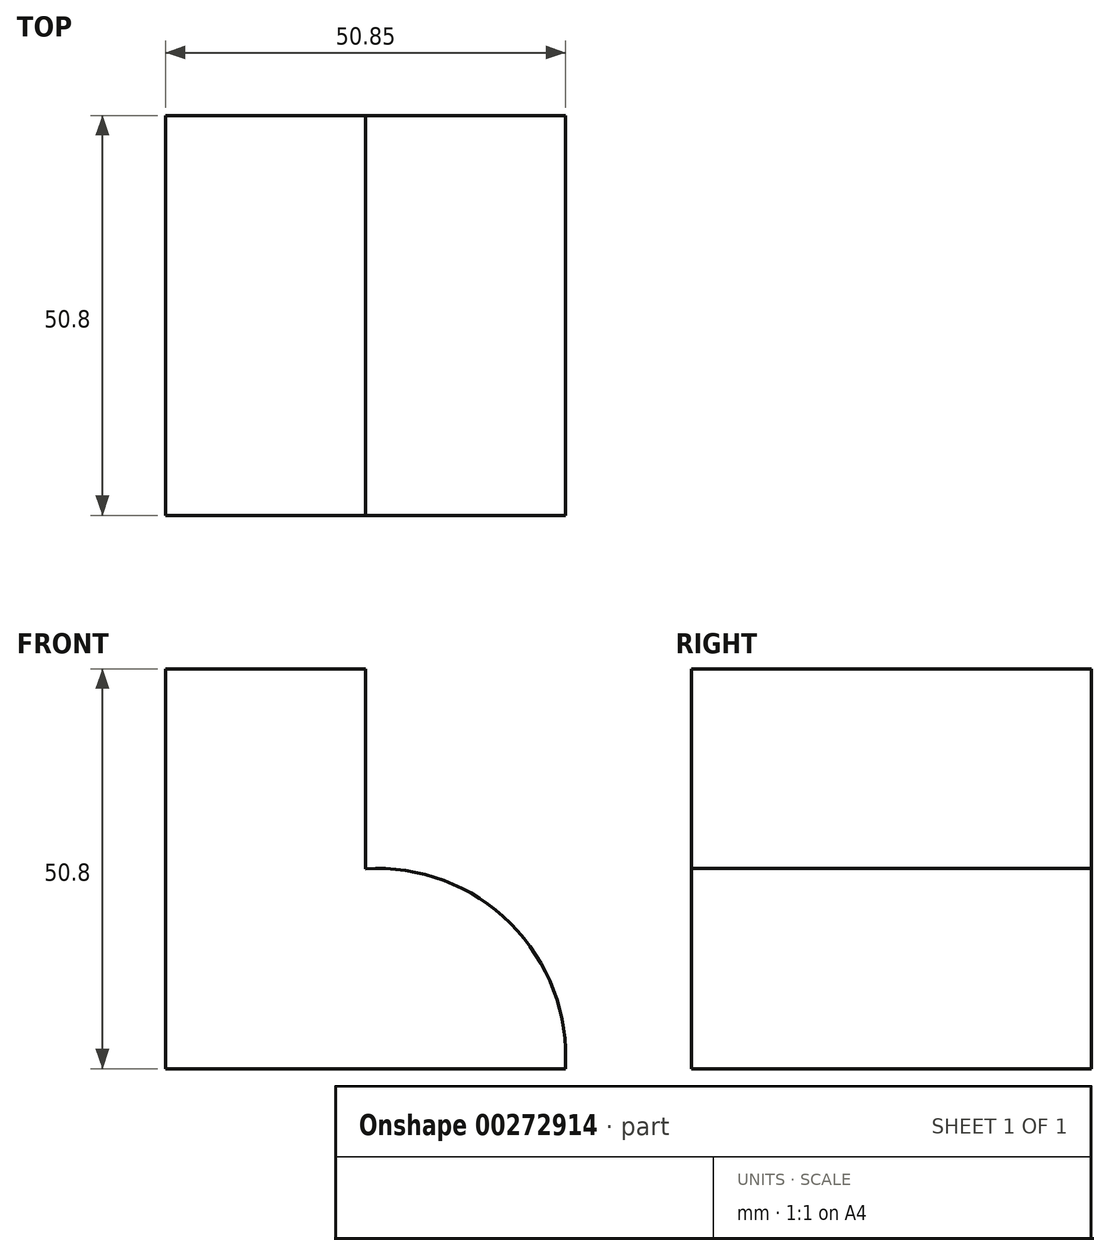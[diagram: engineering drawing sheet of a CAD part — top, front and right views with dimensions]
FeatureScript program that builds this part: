
annotation { "Feature Type Name" : "Feature", "Feature Type Description" : "" }
export const myFeature = defineFeature(function(context is Context, id is Id, definition is map)
    precondition{}
    {
        {
            var Q0;
            Q0=qCreatedBy(makeId("Front.planeOp"),FACE);
            var sketch = newSketch(context, id + "F0", { "sketchPlane" : qUnion([Q0])});
            skLineSegment(sketch, "E0", {"start": v(-46.6, 36.1) * mm, "end": v(-46.6, -14.7) * mm});
            skLineSegment(sketch, "E1", {"start": v(-46.6, -14.7) * mm, "end": v(4.2, -14.7) * mm});
            skLineSegment(sketch, "E2", {"start": v(-46.6, 36.1) * mm, "end": v(-21.2, 36.1) * mm});
            skLineSegment(sketch, "E3", {"start": v(-21.2, 36.1) * mm, "end": v(-21.2, 10.7) * mm});
            skArc(sketch, "E4", {"start": v(4.2, -14.7) * mm, "mid": v(-2.76, 3.73) * mm, "end": v(-21.2, 10.7) * mm});
            skSolve(sketch);
        }
        {
            var Q0;
            Q0=makeQuery(id+"F0.imprint","IMPRINT",FACE,{"disambiguationData":[TD([[makeQuery(id+"F0.imprint","IMPRINT",EDGE,{"derivedFrom":sQuery(id+"F0.wireOp",EDGE,"E0")}),1.0]])]});
            extrude(context, id + "F1", {"entities" : qUnion([Q0]), "depth" : 50.8 * mm});
        }
    });
